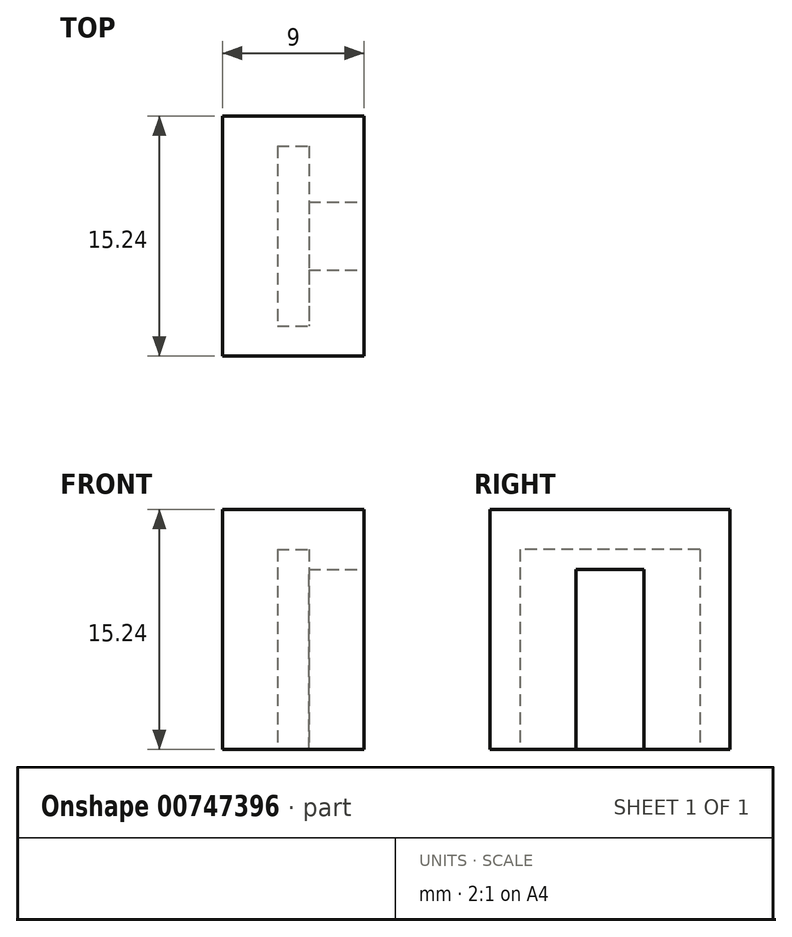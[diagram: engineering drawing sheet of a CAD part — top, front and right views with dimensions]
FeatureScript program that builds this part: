
annotation { "Feature Type Name" : "Feature", "Feature Type Description" : "" }
export const myFeature = defineFeature(function(context is Context, id is Id, definition is map)
    precondition{}
    {
        {
            var Q0;
            Q0=qCreatedBy(makeId("Right.planeOp"),FACE);
            var sketch = newSketch(context, id + "F0", { "sketchPlane" : qUnion([Q0])});
            skLineSegment(sketch, "E0.bottom", {"start": v(0, 0) * mm, "end": v(-15.24, 0) * mm});
            skLineSegment(sketch, "E0.top", {"start": v(0, 15.24) * mm, "end": v(-15.24, 15.24) * mm});
            skLineSegment(sketch, "E0.left", {"start": v(0, 0) * mm, "end": v(0, 15.24) * mm});
            skLineSegment(sketch, "E0.right", {"start": v(-15.24, 0) * mm, "end": v(-15.24, 15.24) * mm});
            skSolve(sketch);
        }
        {
            var Q0;
            Q0=makeQuery(id+"F0.imprint","IMPRINT",FACE,{"disambiguationData":[TD([[makeQuery(id+"F0.imprint","IMPRINT",EDGE,{"derivedFrom":sQuery(id+"F0.wireOp",EDGE,"E0.bottom")}),-1.0]])]});
            extrude(context, id + "F1", {"entities" : qUnion([Q0]), "depth" : 9 * mm, "offsetDistance" : 25.4 * mm});
        }
        {
            var Q0;
            Q0=makeQuery(id+"F1.opExtrude","SWEPT_FACE",FACE,{"disambiguationData":[OSD([sQuery(id+"F0.wireOp",EDGE,"E0.bottom")])]});
            var sketch = newSketch(context, id + "F2", { "sketchPlane" : qUnion([Q0])});
            skLineSegment(sketch, "E1.bottom", {"start": v(3.5, 1.9) * mm, "end": v(5.5, 1.9) * mm});
            skLineSegment(sketch, "E1.top", {"start": v(3.5, 13.34) * mm, "end": v(5.5, 13.34) * mm});
            skLineSegment(sketch, "E1.left", {"start": v(3.5, 1.9) * mm, "end": v(3.5, 13.34) * mm});
            skLineSegment(sketch, "E1.right", {"start": v(5.5, 1.9) * mm, "end": v(5.5, 13.34) * mm});
            skSolve(sketch);
        }
        {
            var Q0;
            Q0=makeQuery(id+"F2.imprint","IMPRINT",FACE,{"disambiguationData":[TD([[makeQuery(id+"F2.imprint","IMPRINT",EDGE,{"derivedFrom":sQuery(id+"F2.wireOp",EDGE,"E1.bottom")}),1.0]])]});
            extrude(context, id + "F3", {"entities" : qUnion([Q0]), "operationType" : NewBodyOperationType.REMOVE, "oppositeDirection" : true, "depth" : 12.7 * mm, "offsetDistance" : 25.4 * mm});
        }
        {
            var Q0;
            Q0=makeQuery(id+"F1.opExtrude","CAP_FACE",FACE,{"disambiguationData":[OSD([sQuery(id+"F0.wireOp",EDGE,"E0.bottom"),sQuery(id+"F0.wireOp",EDGE,"E0.top"),sQuery(id+"F0.wireOp",EDGE,"E0.left"),sQuery(id+"F0.wireOp",EDGE,"E0.right")])],"isStart":false});
            var sketch = newSketch(context, id + "F4", { "sketchPlane" : qUnion([Q0])});
            skLineSegment(sketch, "E2.bottom", {"start": v(-5.46, 0) * mm, "end": v(-9.78, 0) * mm});
            skLineSegment(sketch, "E2.top", {"start": v(-5.46, 11.43) * mm, "end": v(-9.78, 11.43) * mm});
            skLineSegment(sketch, "E2.left", {"start": v(-5.46, 0) * mm, "end": v(-5.46, 11.43) * mm});
            skLineSegment(sketch, "E2.right", {"start": v(-9.78, 0) * mm, "end": v(-9.78, 11.43) * mm});
            skSolve(sketch);
        }
        {
            var Q0;
            Q0=makeQuery(id+"F4.imprint","IMPRINT",FACE,{"disambiguationData":[TD([[makeQuery(id+"F4.imprint","IMPRINT",EDGE,{"derivedFrom":sQuery(id+"F4.wireOp",EDGE,"E2.bottom")}),-1.0]])]});
            extrude(context, id + "F5", {"entities" : qUnion([Q0]), "operationType" : NewBodyOperationType.REMOVE, "oppositeDirection" : true, "depth" : 3.6 * mm, "offsetDistance" : 25.4 * mm});
        }
    });
